# Revit family: LC Duplex 12 fibres
name_source: partatom
category: Installations électriques
units: mm (PartAtom-declared; Revit-internal decimal feet)

## family parameters
Basée sur le plan de construction = Non
Conserver l'orientation des annotations = Non
Cote de connecteur circulaire = Utiliser le diamètre
Couper avec des vides une fois chargée = Non
Partagée = Non
Point de calcul de pièce = Non
Toujours verticalement = Oui
Type d'élément = Normal

## types (4) — shared parameters
Classe ETIM = EC001130
Couleur = IDS_NOIR
Fonction = Panneaux de brassage à connecteur optique Legrand
Hauteur = 23 mm  [stored 0.0754593 ft]
Hauteur de l'ouverture = 6.5 mm
Hauteur des connecteurs = 10 mm  [stored 0.0328084 ft]
IK = IK04
IP = IP20
Largeur (mm) = 108.8 mm  [stored 0.356955 ft]
Largeur de l'ouverture = 6 mm  [stored 0.019685 ft]
Largeur des connecteurs = 13.5 mm  [stored 0.0442913 ft]
Lien e-catalogue = https://www.legrand.fr
Nombre de connecteurs = 12
Profondeur = 38.4 mm  [stored 0.125984 ft]
RAL = 9017
Température de fonctionnement = -10°C à 60°C
Température de stockage = -10°C à 60°C
zero-valued in all types: Elévation par défaut

## per-type parameters (varying)
| type | Couleur des connecteurs | EAN | Libellé BIM | Référence Legrand | Type de connecteur externe | Type de connecteur interne | Type de fibre optique |
| Bloc LC Duplex 12 fibres monomode | IDS_BLEU | 3414970961730 | Bloc LC Duplex 12 fibres monomode | 032114 | LC_DUPLEX | LC_DUPLEX | Monomode |
| Bloc LC APC Duplex 12 fibres monomode | IDS_CYAN | 3414970961778 | Bloc LC APC Duplex 12 fibres monomode | 032116 | LC-DUPLEX | LC-DUPLEX | Monomode |
| Bloc LC Duplex 12 fibres multimode | IDS_JAUNE | 3414970961877 | Bloc LC Duplex 12 fibres multimode | 032124 | LC_DUPLEX | LC_DUPLEX | Multimode |
| Blox LC Duplex(AQUA)_POUR_12_FIBRES_MULTIMODE | IDS_CYAN | 3414971400313 | Bloc LC Duplex aqua 12 fibres multimode | 032137 | LC_DUPLEX | LC_DUPLEX | Multimode |

note: [stored X ft] marks values corroborated as IEEE doubles in the binary element streams (Revit-internal decimal feet)
